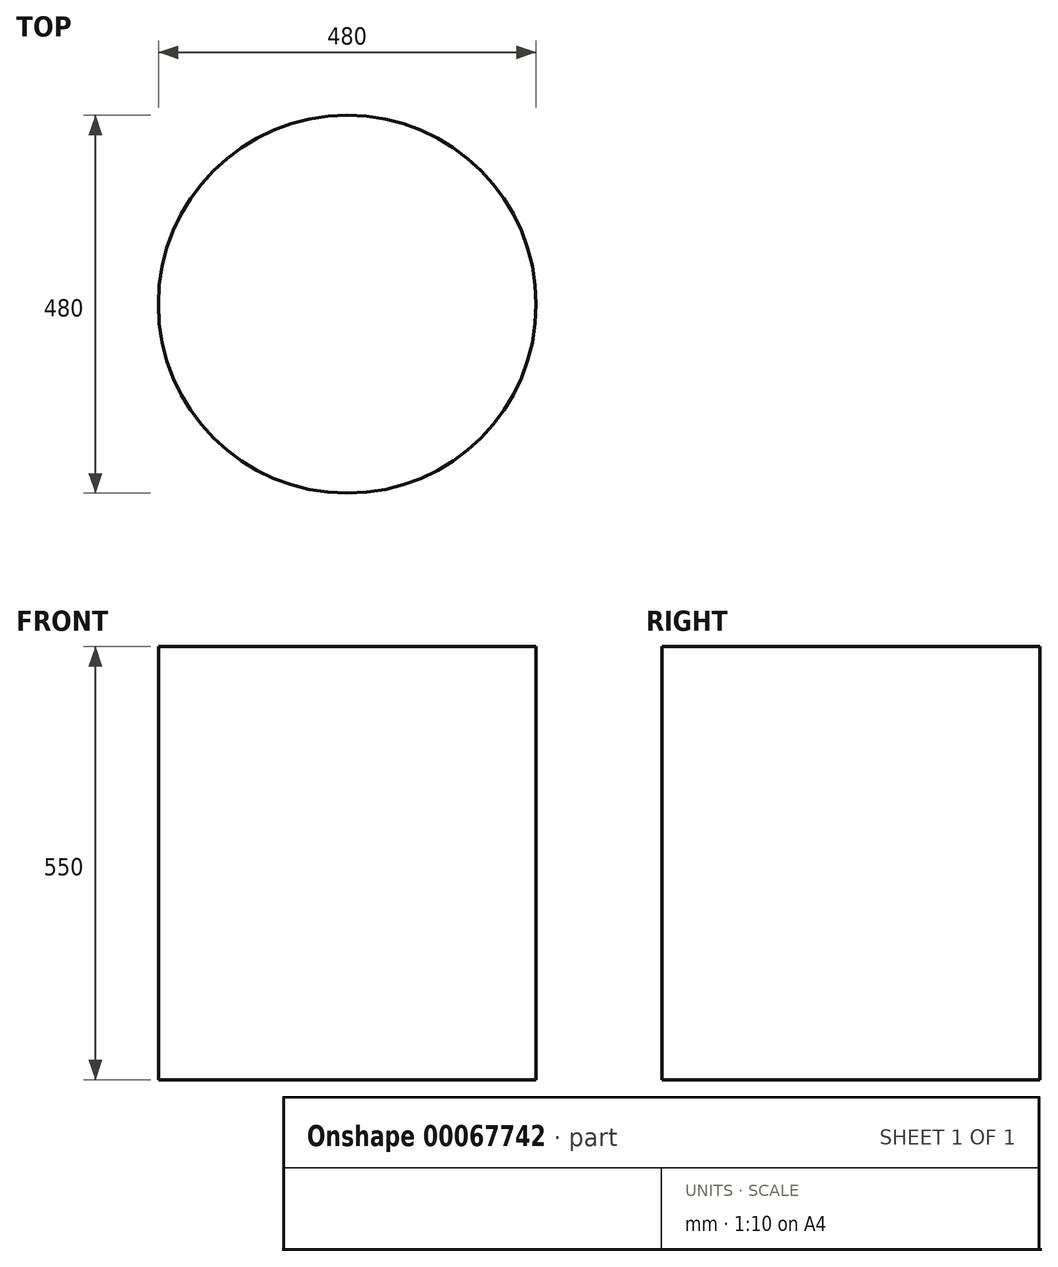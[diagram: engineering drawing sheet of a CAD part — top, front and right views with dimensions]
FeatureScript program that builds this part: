
annotation { "Feature Type Name" : "Feature", "Feature Type Description" : "" }
export const myFeature = defineFeature(function(context is Context, id is Id, definition is map)
    precondition{}
    {
        {
            var Q0;
            Q0=qCreatedBy(makeId("Top.planeOp"),FACE);
            var sketch = newSketch(context, id + "F0", { "sketchPlane" : qUnion([Q0])});
            skCircle(sketch, "E0", {"center": v(0, 0) * mm, "radius": 240 * mm});
            skSolve(sketch);
        }
        {
            var Q0;
            Q0=makeQuery(id+"F0.imprint","IMPRINT",FACE,{"disambiguationData":[TD([[makeQuery(id+"F0.imprint","IMPRINT",EDGE,{"derivedFrom":sQuery(id+"F0.wireOp",EDGE,"E0")}),1.0]])]});
            extrude(context, id + "F1", {"entities" : qUnion([Q0]), "depth" : 550 * mm});
        }
    });
